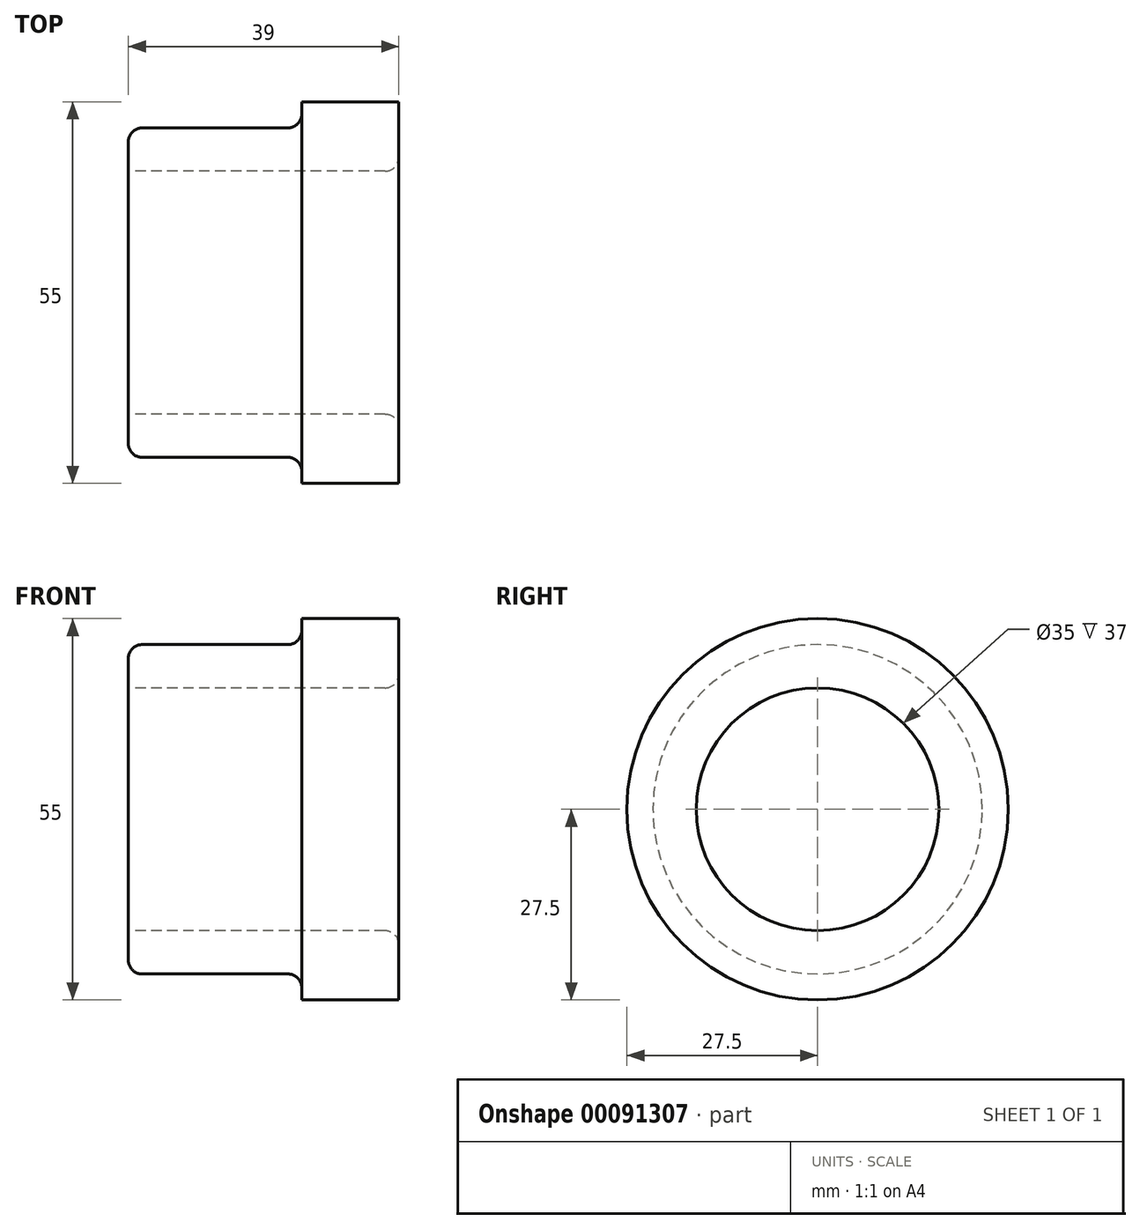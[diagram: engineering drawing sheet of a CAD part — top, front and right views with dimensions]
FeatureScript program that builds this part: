
annotation { "Feature Type Name" : "Feature", "Feature Type Description" : "" }
export const myFeature = defineFeature(function(context is Context, id is Id, definition is map)
    precondition{}
    {
        {
            var Q0;
            Q0=qCreatedBy(makeId("Top.planeOp"),FACE);
            var sketch = newSketch(context, id + "F0", { "sketchPlane" : qUnion([Q0])});
            skLineSegment(sketch, "E0", {"start": v(0, 27.5) * mm, "end": v(-14, 27.5) * mm});
            skLineSegment(sketch, "E1", {"start": v(-14, 27.5) * mm, "end": v(-14, 23.75) * mm});
            skLineSegment(sketch, "E2", {"start": v(-14, 23.75) * mm, "end": v(-39, 23.75) * mm});
            skLineSegment(sketch, "E3", {"start": v(0, 27.5) * mm, "end": v(0, 17.5) * mm});
            skLineSegment(sketch, "E4", {"start": v(-39, 23.75) * mm, "end": v(-39, 17.5) * mm});
            skLineSegment(sketch, "E5", {"start": v(-41.43, 0) * mm, "end": v(19.68, 0) * mm, "construction": true});
            skLineSegment(sketch, "E6", {"start": v(-39, 17.5) * mm, "end": v(0, 17.5) * mm});
            skSolve(sketch);
        }
        {
            var Q0;
            Q0 = qSketchRegion(id + "F0", true);
            var Q1;
            Q1=sQuery(id+"F0.wireOp",EDGE,"E5");
            revolve(context, id + "F1", {"entities" : qUnion([Q0]), "axis" : qUnion([Q1]), "revolveType" : RevolveType.FULL});
        }
        {
            var Q0;
            Q0=makeQuery(id+"F1.opRevolve","SWEPT_EDGE",EDGE,{"disambiguationData":[OSD([sQuery(id+"F0.wireOp",EDGE,"E1"),sQuery(id+"F0.wireOp",EDGE,"E2")])]});
            fillet(context, id + "F2", {"entities" : qUnion([Q0]), "radius" : 2 * mm, "tangentPropagation" : true, "allowEdgeOverflow" : false});
        }
        {
            var Q0;
            Q0=makeQuery(id+"F1.opRevolve","SWEPT_EDGE",EDGE,{"disambiguationData":[OSD([sQuery(id+"F0.wireOp",EDGE,"E2"),sQuery(id+"F0.wireOp",EDGE,"E4")])]});
            var Q1;
            Q1=makeQuery(id+"F1.opRevolve","SWEPT_EDGE",EDGE,{"disambiguationData":[OSD([sQuery(id+"F0.wireOp",EDGE,"E3"),sQuery(id+"F0.wireOp",EDGE,"E6")])]});
            fillet(context, id + "F3", {"entities" : qUnion([Q0, Q1]), "radius" : 2 * mm, "tangentPropagation" : true, "allowEdgeOverflow" : false});
        }
    });
